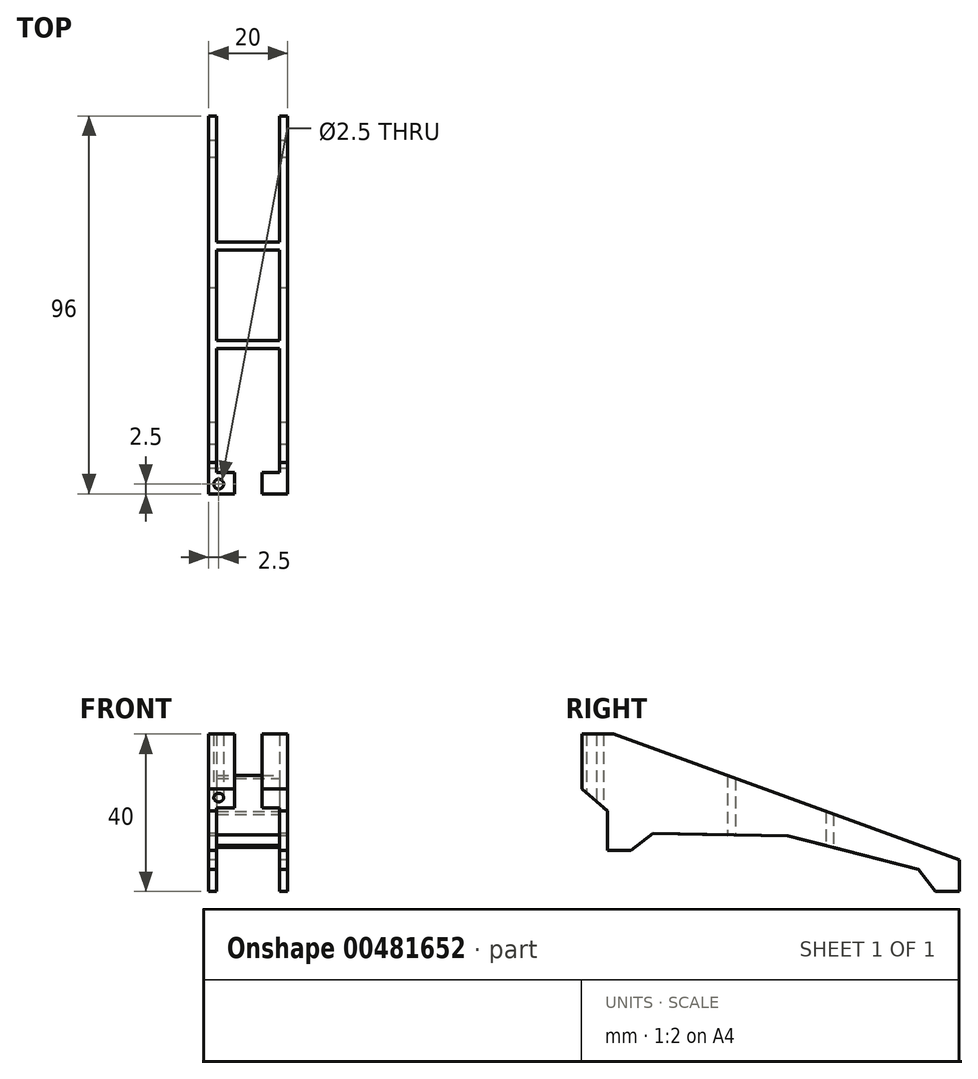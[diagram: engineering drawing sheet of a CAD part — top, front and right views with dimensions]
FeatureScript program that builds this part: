
annotation { "Feature Type Name" : "Feature", "Feature Type Description" : "" }
export const myFeature = defineFeature(function(context is Context, id is Id, definition is map)
    precondition{}
    {
        {
            var Q0;
            Q0=qCreatedBy(makeId("Top.planeOp"),FACE);
            var sketch = newSketch(context, id + "F0", { "sketchPlane" : qUnion([Q0])});
            skLineSegment(sketch, "E0.bottom", {"start": v(10, -45) * mm, "end": v(3.5, -45) * mm});
            skLineSegment(sketch, "E0.top", {"start": v(8, 45) * mm, "end": v(-8, 45) * mm});
            skLineSegment(sketch, "E0.left", {"start": v(10, -45) * mm, "end": v(10, 45) * mm});
            skLineSegment(sketch, "E0.right", {"start": v(-10, -45) * mm, "end": v(-10, 45) * mm});
            skPoint(sketch, "E0.middle", {"position": v(0, 0) * mm});
            skCircle(sketch, "E1", {"center": v(0, 45) * mm, "radius": 14 * mm, "construction": true});
            skLineSegment(sketch, "E2", {"start": v(-8, -8) * mm, "end": v(8, -8) * mm});
            skLineSegment(sketch, "E3", {"start": v(-8, 17) * mm, "end": v(8, 17) * mm});
            skLineSegment(sketch, "E4.0", {"start": v(-8, -39.5) * mm, "end": v(-8, -8) * mm});
            skLineSegment(sketch, "E4.2", {"start": v(8, -39.5) * mm, "end": v(8, -8) * mm});
            skLineSegment(sketch, "E5.0", {"start": v(-8, 19) * mm, "end": v(8, 19) * mm});
            skLineSegment(sketch, "E6.0", {"start": v(-8, -6) * mm, "end": v(8, -6) * mm});
            skLineSegment(sketch, "E7.top", {"start": v(-8, 51) * mm, "end": v(-10, 51) * mm});
            skLineSegment(sketch, "E7.left", {"start": v(-8, 45) * mm, "end": v(-8, 51) * mm});
            skLineSegment(sketch, "E7.right", {"start": v(-10, 45) * mm, "end": v(-10, 51) * mm});
            skLineSegment(sketch, "E8.MirrorCS", {"start": v(8, 51) * mm, "end": v(10, 51) * mm});
            skLineSegment(sketch, "E9.MirrorCS", {"start": v(8, 45) * mm, "end": v(8, 51) * mm});
            skLineSegment(sketch, "E10.MirrorCS", {"start": v(10, 45) * mm, "end": v(10, 51) * mm});
            skLineSegment(sketch, "E11.trimOffspring", {"start": v(8, 19) * mm, "end": v(8, 45) * mm});
            skLineSegment(sketch, "E12.trimOffspring", {"start": v(-8, 19) * mm, "end": v(-8, 45) * mm});
            skLineSegment(sketch, "E13.trimOffspring", {"start": v(-8, -6) * mm, "end": v(-8, 17) * mm});
            skLineSegment(sketch, "E14.trimOffspring", {"start": v(8, -6) * mm, "end": v(8, 17) * mm});
            skLineSegment(sketch, "E15", {"start": v(3.5, -39.5) * mm, "end": v(3.5, -45) * mm});
            skLineSegment(sketch, "E16.MirrorCS", {"start": v(-3.5, -39.5) * mm, "end": v(-3.5, -45) * mm});
            skLineSegment(sketch, "E17.trimOffspring", {"start": v(-3.5, -39.5) * mm, "end": v(-8, -39.5) * mm});
            skLineSegment(sketch, "E18.trimOffspring", {"start": v(-3.5, -45) * mm, "end": v(-10, -45) * mm});
            skLineSegment(sketch, "E19", {"start": v(8, -39.5) * mm, "end": v(3.5, -39.5) * mm});
            skCircle(sketch, "E20", {"center": v(7.5, -42.5) * mm, "radius": 1.25 * mm});
            skCircle(sketch, "E21.MirrorC", {"center": v(-7.5, -42.5) * mm, "radius": 1.25 * mm});
            skSolve(sketch);
        }
        {
            var Q0;
            Q0=makeQuery(id+"F0.imprint","IMPRINT",FACE,{"disambiguationData":[TD([[makeQuery(id+"F0.imprint","IMPRINT",EDGE,{"derivedFrom":sQuery(id+"F0.wireOp",EDGE,"E0.bottom")}),-1.0]])]});
            var Q1;
            Q1=makeQuery(id+"F0.imprint","IMPRINT",FACE,{"disambiguationData":[TD([[makeQuery(id+"F0.imprint","IMPRINT",EDGE,{"derivedFrom":sQuery(id+"F0.wireOp",EDGE,"E21.MirrorC")}),-1.0]])]});
            var Q2;
            Q2=makeQuery(id+"F0.imprint","IMPRINT",FACE,{"disambiguationData":[TD([[makeQuery(id+"F0.imprint","IMPRINT",EDGE,{"derivedFrom":sQuery(id+"F0.wireOp",EDGE,"E20")}),1.0]])]});
            extrude(context, id + "F1", {"entities" : qUnion([Q0, Q1, Q2]), "depth" : 40 * mm, "offsetDistance" : 25 * mm});
        }
        {
            var Q0;
            Q0=makeQuery(id+"F1.opExtrude","SWEPT_FACE",FACE,{"disambiguationData":[OSD([sQuery(id+"F0.wireOp",EDGE,"E0.right"),sQuery(id+"F0.wireOp",EDGE,"E7.right")])]});
            var sketch = newSketch(context, id + "F2", { "sketchPlane" : qUnion([Q0])});
            skLineSegment(sketch, "E22", {"start": v(-51, 40) * mm, "end": v(37, 40) * mm});
            skLineSegment(sketch, "E23", {"start": v(37, 40) * mm, "end": v(-51, 7.97) * mm});
            skLineSegment(sketch, "E24", {"start": v(-51, 7.97) * mm, "end": v(-51, 40) * mm});
            skLineSegment(sketch, "E25", {"start": v(45, 26) * mm, "end": v(38.5, 20.4) * mm});
            skLineSegment(sketch, "E26", {"start": v(38.5, 20.4) * mm, "end": v(38.5, 0) * mm});
            skLineSegment(sketch, "E27", {"start": v(38.5, 0) * mm, "end": v(45, 0) * mm});
            skLineSegment(sketch, "E28", {"start": v(45, 0) * mm, "end": v(45, 26) * mm});
            skLineSegment(sketch, "E29", {"start": v(38.5, 10.4) * mm, "end": v(32.5, 10.4) * mm});
            skLineSegment(sketch, "E30", {"start": v(32.5, 10.4) * mm, "end": v(26.88, 14.69) * mm});
            skLineSegment(sketch, "E31", {"start": v(26.88, 14.69) * mm, "end": v(-7.35, 14.12) * mm});
            skLineSegment(sketch, "E32", {"start": v(-6.5, 19.4) * mm, "end": v(-6.5, 4.65) * mm, "construction": true});
            skLineSegment(sketch, "E33.MirrorCS", {"start": v(-44.8, 0) * mm, "end": v(-40.51, 5.62) * mm});
            skLineSegment(sketch, "E34.MirrorCS", {"start": v(-40.51, 5.62) * mm, "end": v(-7.35, 14.12) * mm});
            skLineSegment(sketch, "E35.0", {"start": v(27.54, 9.73) * mm, "end": v(32.5, 10.4) * mm, "construction": true});
            skLineSegment(sketch, "E35.1", {"start": v(27.54, 9.73) * mm, "end": v(26.88, 14.69) * mm, "construction": true});
            skLineSegment(sketch, "E35.9", {"start": v(-6.82, 10.15) * mm, "end": v(26.88, 14.69) * mm, "construction": true});
            skLineSegment(sketch, "E35.10", {"start": v(-6.82, 10.15) * mm, "end": v(-7.35, 14.12) * mm, "construction": true});
            skLineSegment(sketch, "E36", {"start": v(-44.8, 0) * mm, "end": v(24.1, -28.11) * mm});
            skLineSegment(sketch, "E37", {"start": v(24.1, -28.11) * mm, "end": v(60, -8.65) * mm});
            skLineSegment(sketch, "E38", {"start": v(60, -8.65) * mm, "end": v(45, 26) * mm});
            skSolve(sketch);
        }
        {
            var Q0;
            Q0=makeQuery(id+"F2.imprint","IMPRINT",FACE,{"disambiguationData":[TD([[makeQuery(id+"F2.imprint","IMPRINT",EDGE,{"derivedFrom":sQuery(id+"F2.wireOp",EDGE,"E22")}),1.0]])]});
            var Q1;
            {var subQ0=sQuery(id+"F2.wireOp",EDGE,"E29");Q1=makeQuery(id+"F2.imprint","IMPRINT",FACE,{"disambiguationData":[TD([[makeQuery(id+"F2.imprint","IMPRINT",EDGE,{"derivedFrom":subQ0}),1.0]])]});}
            var Q2;
            {var subQ3=sQuery(id+"F2.wireOp",EDGE,"E25");Q2=makeQuery(id+"F2.imprint","IMPRINT",FACE,{"disambiguationData":[TD([[makeQuery(id+"F2.imprint","IMPRINT",EDGE,{"derivedFrom":subQ3}),1.0]])]});}
            extrude(context, id + "F3", {"entities" : qUnion([Q0, Q1, Q2]), "operationType" : NewBodyOperationType.REMOVE, "oppositeDirection" : true, "depth" : 50 * mm, "offsetDistance" : 25 * mm});
        }
    });
